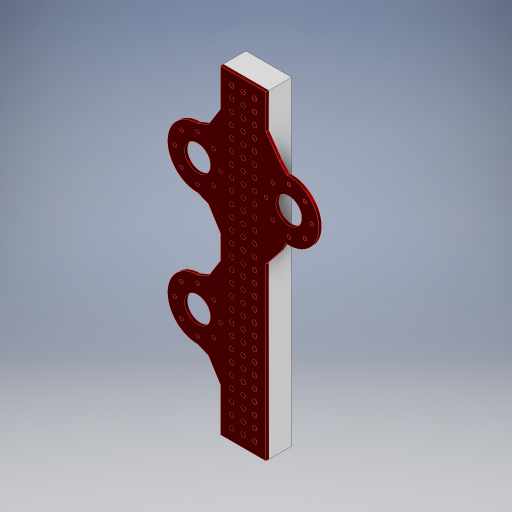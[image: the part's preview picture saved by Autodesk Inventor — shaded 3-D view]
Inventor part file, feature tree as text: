
AUTODESK INVENTOR PART (.ipt)
format: ipt  version: 2024.2 (Build 282272000, 272)  size: 666,112 bytes
history: native  units: in
note: dims shown in document units (in); Inventor stores cm internally (conversion verified against a paired STEP export)
features: extrude x3, sketch x3, projected_geometry x1, other x1
ambient origin geometry x8: Origin, YZ Plane, XZ Plane, XY Plane, X Axis, Y Axis, Z Axis, Center Point
bodies: Solid1 (feature_tree)
feature tree (8):
  extrude  "Extrusion1"  Depth=1.0in
  extrude  "Extrusion2"  Depth=14.0in
  extrude  "Extrusion3"  Depth=0.125in
  sketch  "Sketch1"  dims[d0=2.0in d1=1.0in]
  sketch  "Sketch2"  dims[d2=14.0in d3=0.0in d4=0.196in]
  sketch  "Sketch3"  dims[d5=0.5in d6=0.5in d7=1.1811in d9=0.5in d10=10.6299in d12=0.5in d15=14.0in d16=0.0in d17=1.125in d18=4.0in d19=1.125in d20=4.0in d21=4.0in d22=1.0in d23=1.125in d24=5.75in d25=0.159in d26=0.159in d27=2.0in d28=1.0in d33=1.0in d34=1.5748in d36=360.0deg d38=0.159in d39=1.0in d40=1.5748in d42=360.0deg d44=0.75in d45=0.75in d46=0.75in d47=0.5in d48=1.0in d49=0.5in d50=1.0in d51=0.5in d52=1.0in d53=0.5in d54=1.0in d56=1.0in d57=0.5in d58=1.0in d59=0.125in d60=0.0in d61=3.1496in d63=360.0deg d65=3.1496in d67=360.0deg d73=3.1496in d75=360.0deg]
  projected_geometry  "Projected Loop1"
  other  "2024-210-009-Shooter-Gusset-Plate"
